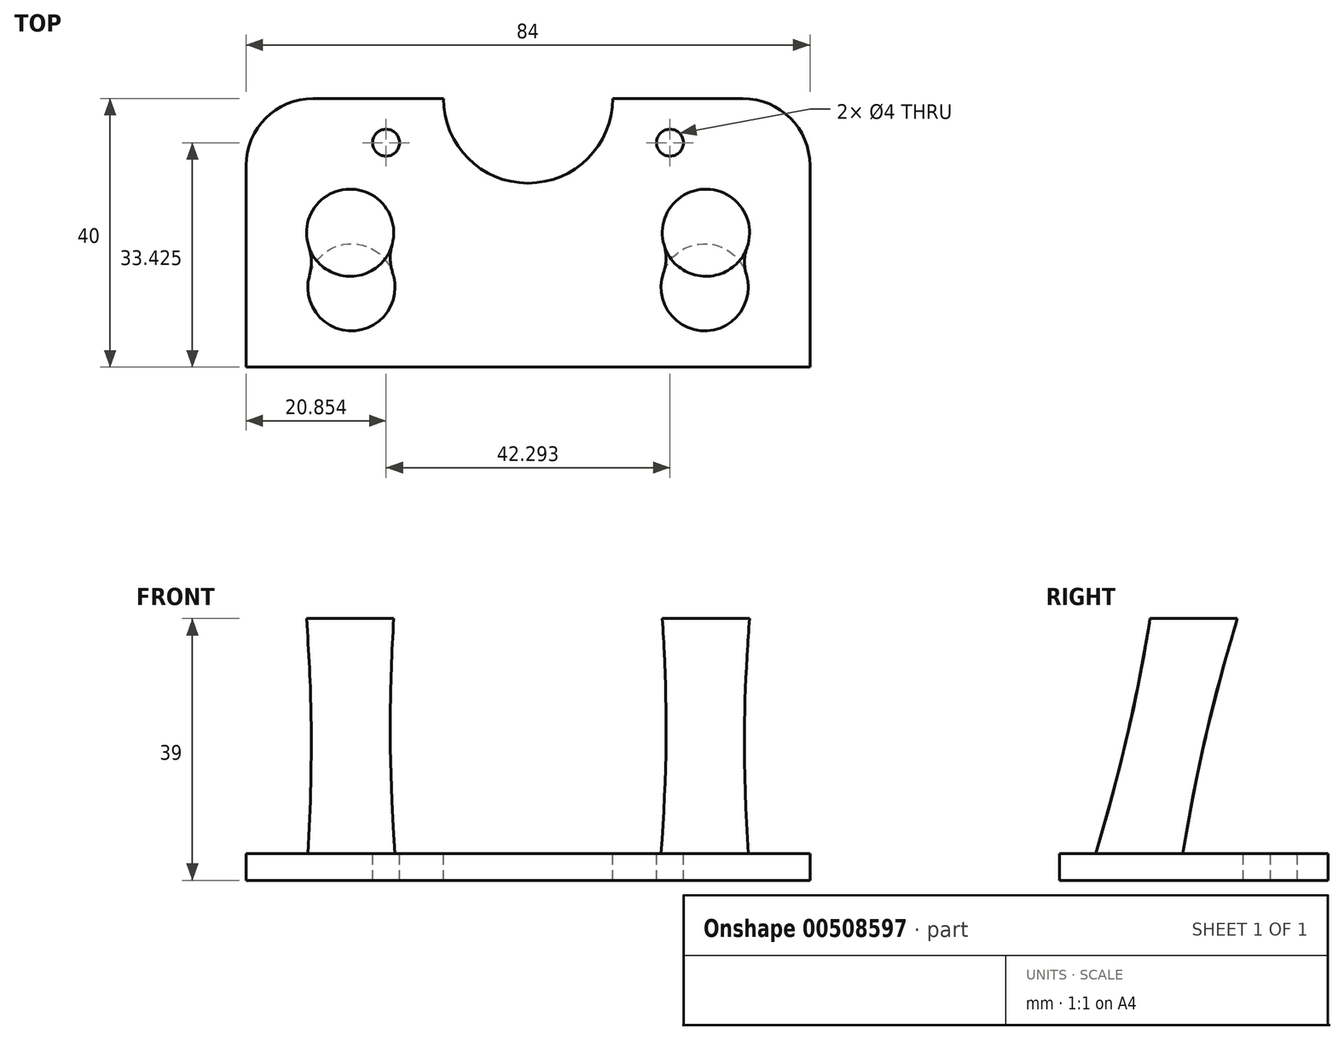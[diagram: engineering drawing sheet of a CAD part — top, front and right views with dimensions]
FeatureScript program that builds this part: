
annotation { "Feature Type Name" : "Feature", "Feature Type Description" : "" }
export const myFeature = defineFeature(function(context is Context, id is Id, definition is map)
    precondition{}
    {
        {
            var Q0;
            Q0=qCreatedBy(makeId("Top.planeOp"),FACE);
            var sketch = newSketch(context, id + "F0", { "sketchPlane" : qUnion([Q0])});
            skLineSegment(sketch, "E0.bottom", {"start": v(-42, -20) * mm, "end": v(42, -20) * mm});
            skLineSegment(sketch, "E0.top", {"start": v(-32, 20) * mm, "end": v(-12.6, 20) * mm});
            skLineSegment(sketch, "E0.left", {"start": v(-42, -20) * mm, "end": v(-42, 10) * mm});
            skLineSegment(sketch, "E0.right", {"start": v(42, -20) * mm, "end": v(42, 10) * mm});
            skPoint(sketch, "E0.middle", {"position": v(0, 0) * mm});
            skCircle(sketch, "E1", {"center": v(26.3, -8.13) * mm, "radius": 6.5 * mm});
            skCircle(sketch, "E2", {"center": v(-26.3, -8.13) * mm, "radius": 6.5 * mm});
            skPoint(sketch, "E3.visualSharp", {"position": v(-42, 20) * mm});
            skArc(sketch, "E3.filletArc", {"start": v(-32, 20) * mm, "mid": v(-39.07, 17.07) * mm, "end": v(-42, 10) * mm});
            skPoint(sketch, "E4.visualSharp", {"position": v(42, 20) * mm});
            skArc(sketch, "E4.filletArc", {"start": v(42, 10) * mm, "mid": v(39.07, 17.07) * mm, "end": v(32, 20) * mm});
            skArc(sketch, "E5", {"start": v(-12.6, 20) * mm, "mid": v(0, 7.4) * mm, "end": v(12.6, 20) * mm});
            skLineSegment(sketch, "E6.trimOffspring", {"start": v(12.6, 20) * mm, "end": v(32, 20) * mm});
            skCircle(sketch, "E7", {"center": v(21.15, 13.43) * mm, "radius": 2 * mm});
            skCircle(sketch, "E8.MirrorC", {"center": v(-21.15, 13.43) * mm, "radius": 2 * mm});
            skSolve(sketch);
        }
        {
            var Q0;
            Q0=qCreatedBy(makeId("Top.planeOp"),FACE);
            cPlane(context, id + "F1", {"entities" : qUnion([Q0]), "cplaneType" : CPlaneType.OFFSET, "offset" : 35 * mm, "width" : 150 * mm, "height" : 150 * mm});
        }
        {
            var Q0;
            Q0=qCreatedBy(id+"F1.planeOp",FACE);
            var sketch = newSketch(context, id + "F2", { "sketchPlane" : qUnion([Q0])});
            skCircle(sketch, "E9", {"center": v(-26.5, 0) * mm, "radius": 6.5 * mm});
            skCircle(sketch, "E10", {"center": v(26.5, 0) * mm, "radius": 6.5 * mm});
            skSolve(sketch);
        }
        {
            var Q0;
            Q0=makeQuery(id+"F0.imprint","IMPRINT",FACE,{"disambiguationData":[TD([[makeQuery(id+"F0.imprint","IMPRINT",EDGE,{"derivedFrom":sQuery(id+"F0.wireOp",EDGE,"E0.bottom")}),1.0]])]});
            extrude(context, id + "F3", {"entities" : qUnion([Q0]), "depth" : -4 * mm});
        }
        {
            var Q0;
            Q0=makeQuery(id+"F0.imprint","IMPRINT",FACE,{"disambiguationData":[TD([[makeQuery(id+"F0.imprint","IMPRINT",EDGE,{"derivedFrom":sQuery(id+"F0.wireOp",EDGE,"E2")}),1.0]])]});
            var Q1;
            Q1=makeQuery(id+"F2.imprint","IMPRINT",FACE,{"disambiguationData":[TD([[makeQuery(id+"F2.imprint","IMPRINT",EDGE,{"derivedFrom":sQuery(id+"F2.wireOp",EDGE,"E9")}),1.0]])]});
            loft(context, id + "F4", {"sheetProfilesArray" : [{ "sheetProfileEntities" : qUnion([Q0]) }, { "sheetProfileEntities" : qUnion([Q1]) }]});
        }
        {
            var Q0;
            Q0=makeQuery(id+"F0.imprint","IMPRINT",FACE,{"disambiguationData":[TD([[makeQuery(id+"F0.imprint","IMPRINT",EDGE,{"derivedFrom":sQuery(id+"F0.wireOp",EDGE,"E1")}),1.0]])]});
            var Q1;
            Q1=makeQuery(id+"F2.imprint","IMPRINT",FACE,{"disambiguationData":[TD([[makeQuery(id+"F2.imprint","IMPRINT",EDGE,{"derivedFrom":sQuery(id+"F2.wireOp",EDGE,"E10")}),1.0]])]});
            loft(context, id + "F5", {"sheetProfilesArray" : [{ "sheetProfileEntities" : qUnion([Q0]) }, { "sheetProfileEntities" : qUnion([Q1]) }]});
        }
        {
            var Q0;
            Q0=makeQuery(id+"F0.imprint","IMPRINT",FACE,{"disambiguationData":[TD([[makeQuery(id+"F0.imprint","IMPRINT",EDGE,{"derivedFrom":sQuery(id+"F0.wireOp",EDGE,"E2")}),1.0]])]});
            var Q1;
            Q1=makeQuery(id+"F0.imprint","IMPRINT",FACE,{"disambiguationData":[TD([[makeQuery(id+"F0.imprint","IMPRINT",EDGE,{"derivedFrom":sQuery(id+"F0.wireOp",EDGE,"E1")}),1.0]])]});
            extrude(context, id + "F6", {"entities" : qUnion([Q0, Q1]), "operationType" : NewBodyOperationType.ADD, "depth" : -4 * mm});
        }
    });
